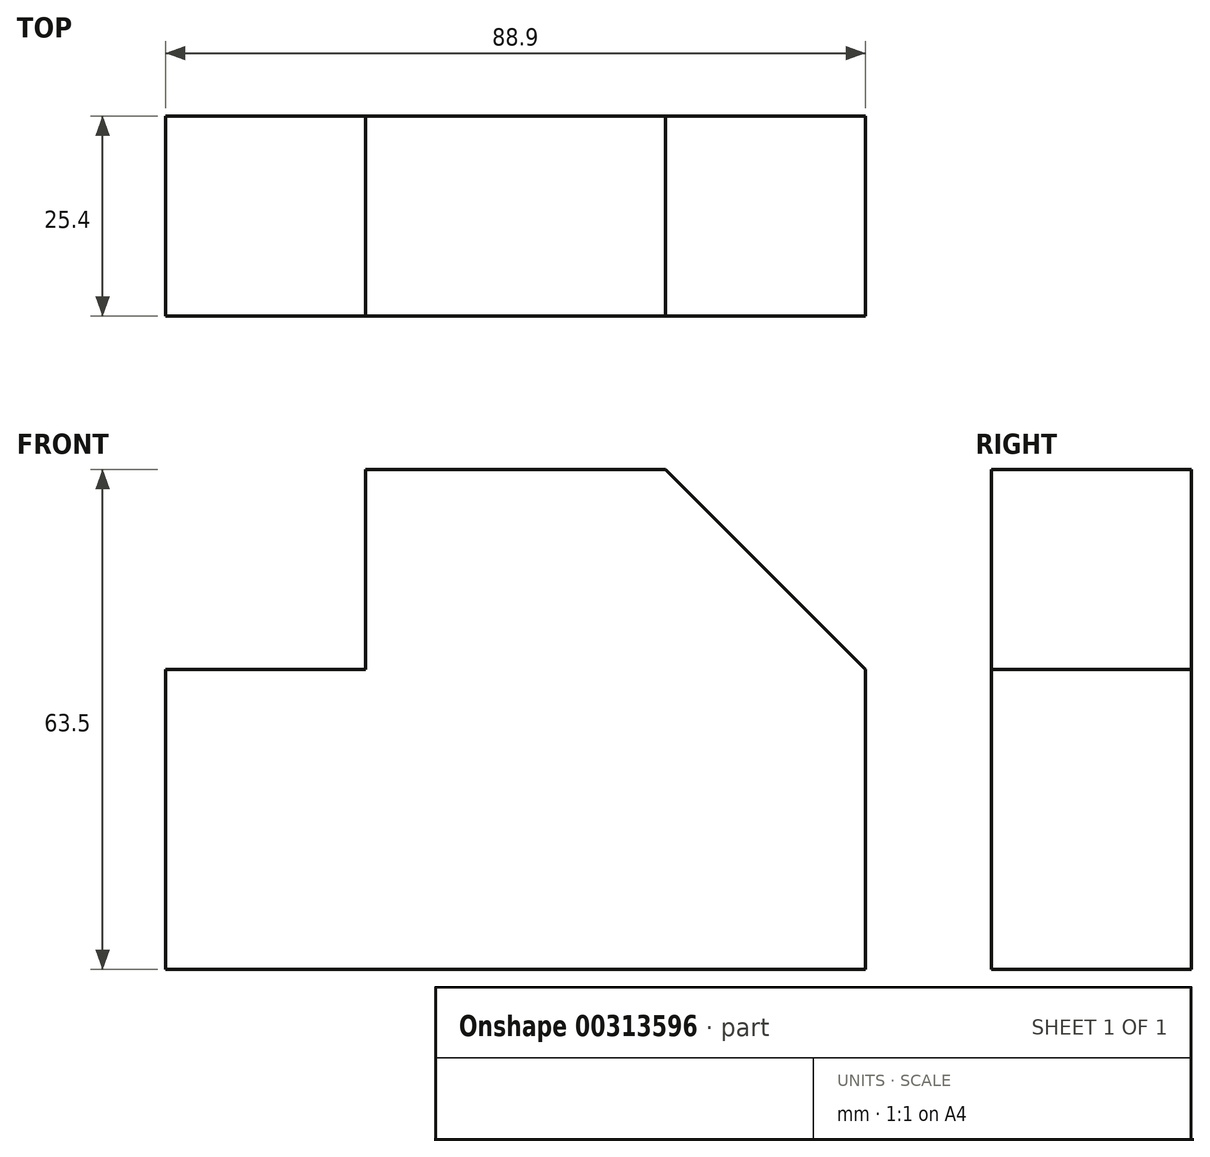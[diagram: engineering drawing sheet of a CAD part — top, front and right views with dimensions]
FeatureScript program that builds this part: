
annotation { "Feature Type Name" : "Feature", "Feature Type Description" : "" }
export const myFeature = defineFeature(function(context is Context, id is Id, definition is map)
    precondition{}
    {
        {
            var Q0;
            Q0=qCreatedBy(makeId("Front.planeOp"),FACE);
            var sketch = newSketch(context, id + "F0", { "sketchPlane" : qUnion([Q0])});
            skLineSegment(sketch, "E0", {"start": v(-41.5, -39.93) * mm, "end": v(47.4, -39.93) * mm});
            skLineSegment(sketch, "E1", {"start": v(47.4, -39.93) * mm, "end": v(47.4, -1.83) * mm});
            skLineSegment(sketch, "E2", {"start": v(47.4, -1.83) * mm, "end": v(22, 23.57) * mm});
            skLineSegment(sketch, "E3", {"start": v(22, 23.57) * mm, "end": v(-16.1, 23.57) * mm});
            skLineSegment(sketch, "E4", {"start": v(-16.1, 23.57) * mm, "end": v(-16.1, -1.83) * mm});
            skLineSegment(sketch, "E5", {"start": v(-16.1, -1.83) * mm, "end": v(-41.5, -1.83) * mm});
            skLineSegment(sketch, "E6", {"start": v(-41.5, -1.83) * mm, "end": v(-41.5, -39.93) * mm});
            skSolve(sketch);
        }
        {
            var Q0;
            Q0=makeQuery(id+"F0.imprint","IMPRINT",FACE,{"disambiguationData":[TD([[makeQuery(id+"F0.imprint","IMPRINT",EDGE,{"derivedFrom":sQuery(id+"F0.wireOp",EDGE,"E0")}),1.0]])]});
            extrude(context, id + "F1", {"entities" : qUnion([Q0]), "depth" : 25.4 * mm});
        }
    });
